# Revit family: 22023
name_source: partatom
category: Luminarias
units: mm (PartAtom-declared; Revit-internal decimal feet)

## family parameters
Compartido = No
Corte con vacíos al cargar = Sí
Cota de conector redondo = Diámetro de uso
Número OmniClass = 23.80.70.00
Origen de luz = No
Punto de cálculo de habitación = No
Se basa en plano de trabajo = Sí
Siempre vertical = No
Tipo de pieza = Normal
Título OmniClass = Lighting

## types (3) — shared parameters
Elevación por defecto = 1219 mm
FARO_Category = Indoor
FARO_Last Actualization Date = 28/10/2024
FARO_Material_01 = FARO_Black_
FARO_Material_03 = FARO_White_translucide
FARO_Model Line = NINA
FARO_Subcategory = Suspended
Fabricante = FARO Barcelona
LAMP 1 = Sí
LAMP 2 = No
Lámpara = 1XE27 MAX 15W LED
URL = https://www.faro.es
Voltage = 100-240 V

## per-type parameters (varying)
| type | FARO_Description EN | FARO_Description ES | FARO_Material_02 | FARO_Ref |
| 22023 NINA Suspended black | NINA Suspended black | NINA Colgante negro | FARO_Black_ | 22023 |
| 22024 NINA Suspended white | NINA Suspended white | NINA Colgante blanco | FARO_White | 22024 |
| 22025 NINA Suspended gold | NINA Suspended gold | NINA Colgante oro | FARO_Gold | 22025 |

## geometry (parser evidence)
native form markers: Sweep x6
no freeform markers — native parametric forms only
